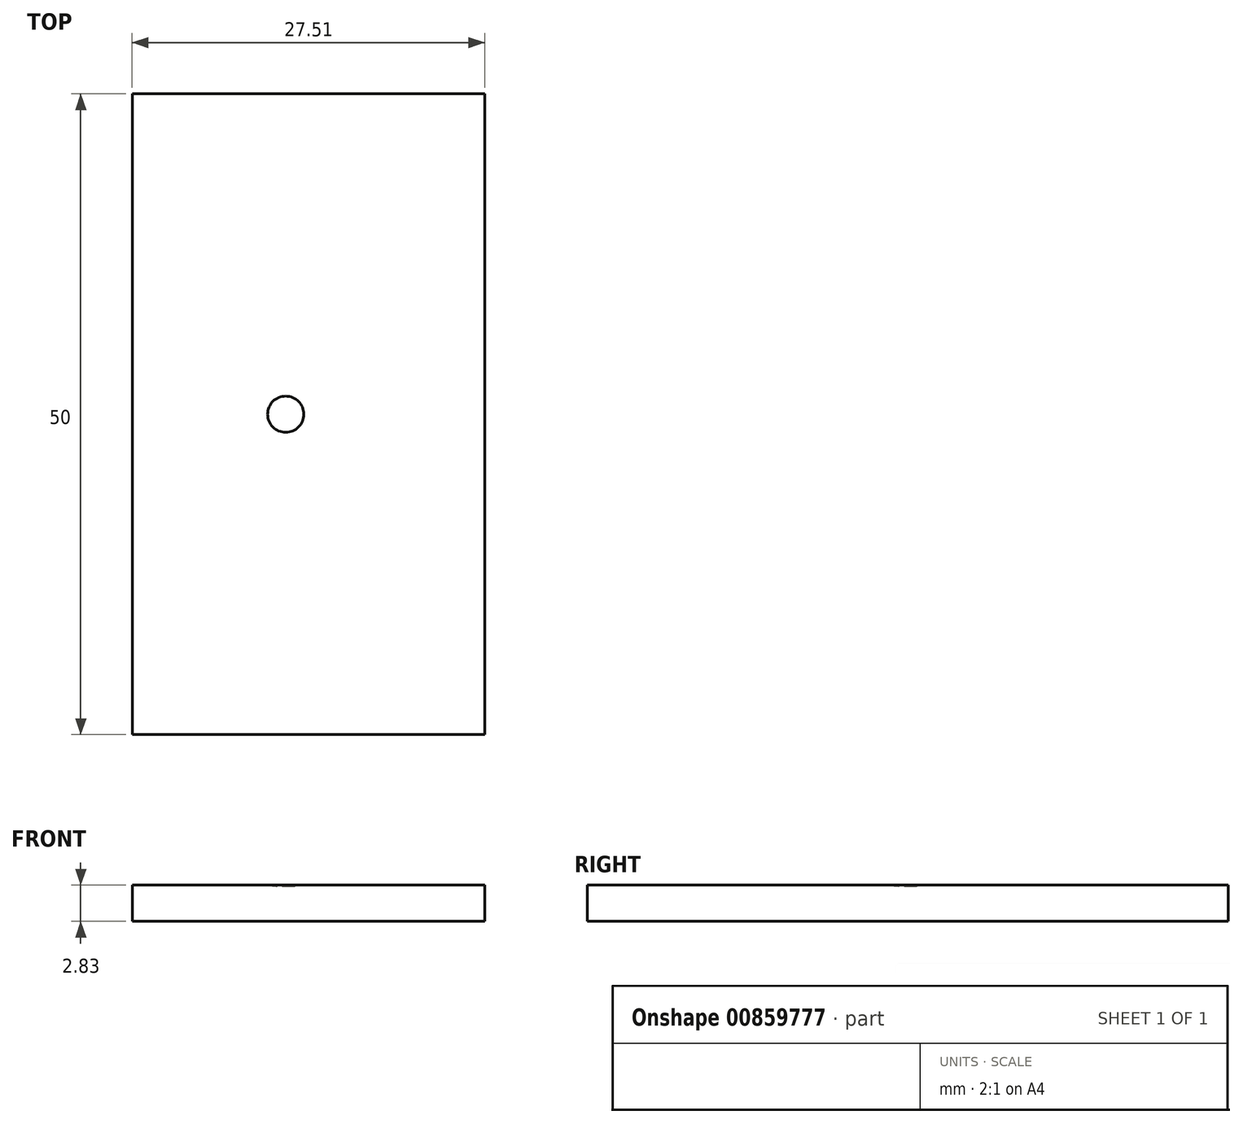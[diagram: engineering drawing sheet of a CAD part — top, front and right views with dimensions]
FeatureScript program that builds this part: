
annotation { "Feature Type Name" : "Feature", "Feature Type Description" : "" }
export const myFeature = defineFeature(function(context is Context, id is Id, definition is map)
    precondition{}
    {
        {
            var Q0;
            Q0=qCreatedBy(makeId("Front.planeOp"),FACE);
            var sketch = newSketch(context, id + "F0", { "sketchPlane" : qUnion([Q0])});
            skArc(sketch, "E0", {"start": v(0, -10) * mm, "mid": v(10, 0) * mm, "end": v(0, 10) * mm});
            skLineSegment(sketch, "E1", {"start": v(0, -10) * mm, "end": v(0, 10) * mm});
            skSolve(sketch);
        }
        {
            var Q0;
            Q0=makeQuery(id+"F0.imprint","IMPRINT",FACE,{"disambiguationData":[TD([[makeQuery(id+"F0.imprint","IMPRINT",EDGE,{"derivedFrom":sQuery(id+"F0.wireOp",EDGE,"E0")}),1.0]])]});
            var Q1;
            Q1=sQuery(id+"F0.wireOp",EDGE,"E1");
            revolve(context, id + "F1", {"surfaceOperationType" : NewSurfaceOperationType.NEW, "entities" : qUnion([Q0]), "axis" : qUnion([Q1]), "revolveType" : RevolveType.FULL});
        }
        {
            var Q0;
            Q0=qCreatedBy(makeId("Front.planeOp"),FACE);
            cPlane(context, id + "F2", {"entities" : qUnion([Q0]), "cplaneType" : CPlaneType.OFFSET, "offset" : 25 * mm, "width" : 150 * mm, "height" : 150 * mm});
        }
        {
            var Q0;
            Q0=qCreatedBy(id+"F2.planeOp",FACE);
            var sketch = newSketch(context, id + "F3", { "sketchPlane" : qUnion([Q0])});
            skCircle(sketch, "E2", {"center": v(0, 0) * mm, "radius": 10 * mm, "construction": true});
            skLineSegment(sketch, "E3", {"start": v(-11.98, -9.9) * mm, "end": v(-11.98, -12.73) * mm});
            skPoint(sketch, "E4.start.orphan", {"position": v(0, -10) * mm});
            skLineSegment(sketch, "E5", {"start": v(-11.98, -12.73) * mm, "end": v(15.53, -12.73) * mm});
            skLineSegment(sketch, "E6", {"start": v(15.53, -12.73) * mm, "end": v(15.53, -9.9) * mm});
            skLineSegment(sketch, "E7.0", {"start": v(-11.98, -9.9) * mm, "end": v(15.53, -9.9) * mm});
            skPoint(sketch, "E8.orphan", {"position": v(15.53, -8) * mm});
            skSolve(sketch);
        }
        {
            var Q0;
            Q0=makeQuery(id+"F3.imprint","IMPRINT",FACE,{"disambiguationData":[TD([[makeQuery(id+"F3.imprint","IMPRINT",EDGE,{"derivedFrom":sQuery(id+"F3.wireOp",EDGE,"E3")}),1.0]])]});
            extrude(context, id + "F4", {"entities" : qUnion([Q0]), "oppositeDirection" : true, "depth" : 50 * mm, "offsetDistance" : 25 * mm});
        }
        {
            var Q0;
            Q0=makeQuery(id+"F1.opRevolve","SWEPT_BODY",BODY,{"disambiguationData":[OSD([sQuery(id+"F0.wireOp",EDGE,"E0"),sQuery(id+"F0.wireOp",EDGE,"E1")])]});
            var Q1;
            Q1=makeQuery(id+"F4.opExtrude","SWEPT_BODY",BODY,{"disambiguationData":[OSD([sQuery(id+"F3.wireOp",EDGE,"f7ecb5c3-e641-4037-9801-33e4b5eb869e.0"),sQuery(id+"F3.wireOp",EDGE,"E3"),sQuery(id+"F3.wireOp",EDGE,"E5"),sQuery(id+"F3.wireOp",EDGE,"E6")])]});
            booleanBodies(context, id + "F5", {"operationType" : BooleanOperationType.SUBTRACTION, "tools" : qUnion([Q0]), "targets" : qUnion([Q1])});
        }
    });
